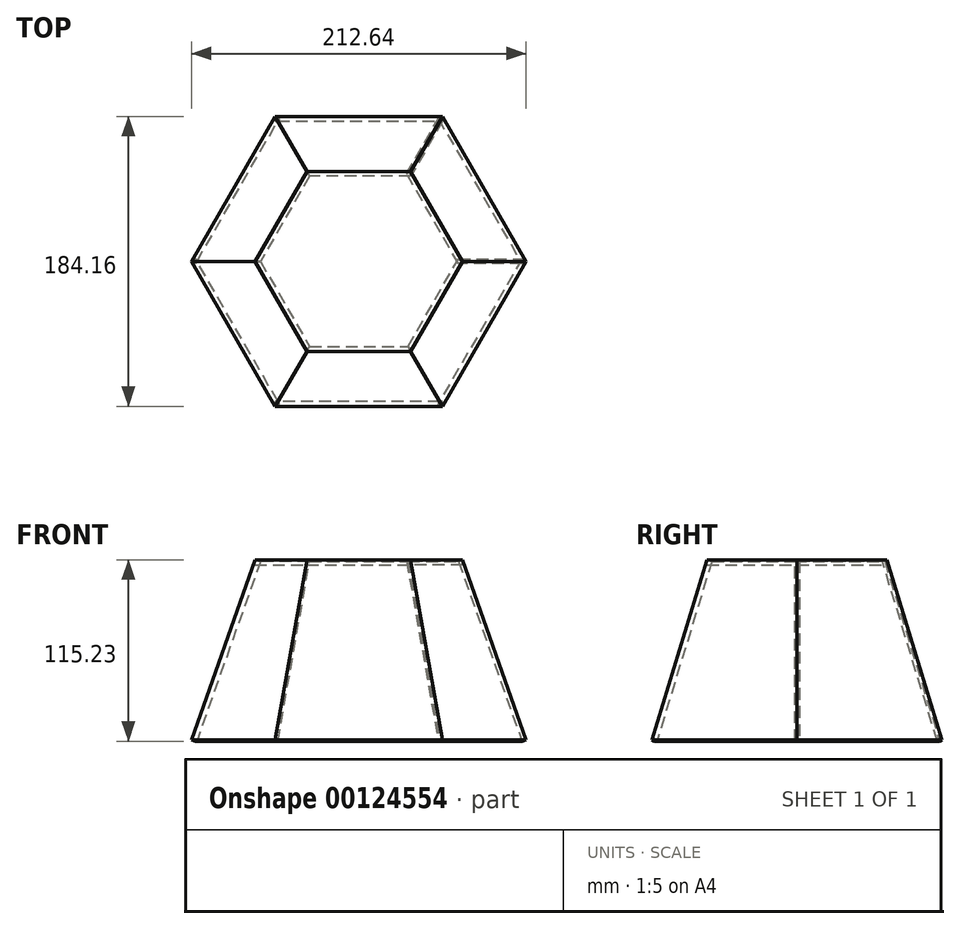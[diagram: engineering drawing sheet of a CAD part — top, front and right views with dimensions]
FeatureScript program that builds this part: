
annotation { "Feature Type Name" : "Feature", "Feature Type Description" : "" }
export const myFeature = defineFeature(function(context is Context, id is Id, definition is map)
    precondition{}
    {
        {
            var Q0;
            Q0=qCreatedBy(makeId("Top.planeOp"),FACE);
            var sketch = newSketch(context, id + "F0", { "sketchPlane" : qUnion([Q0])});
            skCircle(sketch, "E0.cCircle", {"center": v(0, 0) * mm, "radius": 92.08 * mm, "construction": true});
            skLineSegment(sketch, "E0.0", {"start": v(-53.16, 92.08) * mm, "end": v(53.16, 92.08) * mm});
            skLineSegment(sketch, "E0.1", {"start": v(53.16, 92.08) * mm, "end": v(106.32, 0) * mm});
            skLineSegment(sketch, "E0.2", {"start": v(106.32, 0) * mm, "end": v(53.16, -92.07) * mm});
            skLineSegment(sketch, "E0.3", {"start": v(53.16, -92.07) * mm, "end": v(-53.16, -92.08) * mm});
            skLineSegment(sketch, "E0.4", {"start": v(-53.16, -92.08) * mm, "end": v(-106.32, 0) * mm});
            skLineSegment(sketch, "E0.5", {"start": v(-106.32, 0) * mm, "end": v(-53.16, 92.07) * mm});
            skPoint(sketch, "E0.0.midPoint", {"position": v(0, 92.08) * mm});
            skSolve(sketch);
        }
        {
            var Q0;
            Q0=makeQuery(id+"F0.imprint","IMPRINT",FACE,{"disambiguationData":[TD([[makeQuery(id+"F0.imprint","IMPRINT",EDGE,{"derivedFrom":sQuery(id+"F0.wireOp",EDGE,"E0.0")}),-1.0]])]});
            cPlane(context, id + "F1", {"entities" : qUnion([Q0]), "cplaneType" : CPlaneType.OFFSET, "offset" : 114.3 * mm, "width" : 152.4 * mm, "height" : 152.4 * mm});
        }
        {
            var Q0;
            Q0=qCreatedBy(id+"F1.planeOp",FACE);
            var sketch = newSketch(context, id + "F2", { "sketchPlane" : qUnion([Q0])});
            skCircle(sketch, "E1.cCircle", {"center": v(0, 0) * mm, "radius": 57.15 * mm, "construction": true});
            skLineSegment(sketch, "E1.0", {"start": v(-33, 57.15) * mm, "end": v(33, 57.15) * mm});
            skLineSegment(sketch, "E1.1", {"start": v(33, 57.15) * mm, "end": v(66, 0) * mm});
            skLineSegment(sketch, "E1.2", {"start": v(66, 0) * mm, "end": v(33, -57.15) * mm});
            skLineSegment(sketch, "E1.3", {"start": v(33, -57.15) * mm, "end": v(-33, -57.15) * mm});
            skLineSegment(sketch, "E1.4", {"start": v(-33, -57.15) * mm, "end": v(-66, 0) * mm});
            skLineSegment(sketch, "E1.5", {"start": v(-66, 0) * mm, "end": v(-33, 57.15) * mm});
            skPoint(sketch, "E1.0.midPoint", {"position": v(0, 57.15) * mm});
            skSolve(sketch);
        }
        {
            var Q0;
            Q0=sQuery(id+"F0.wireOp",VERTEX,"E0.4.start");
            var Q1;
            Q1=sQuery(id+"F2.wireOp",VERTEX,"E1.4.start");
            var Q2;
            Q2=sQuery(id+"F2.wireOp",VERTEX,"E1.2.end");
            cPlane(context, id + "F3", {"entities" : qUnion([Q0, Q1, Q2]), "cplaneType" : CPlaneType.THREE_POINT, "offset" : 25.4 * mm, "width" : 152.4 * mm, "height" : 152.4 * mm});
        }
        {
            var Q0;
            Q0=qCreatedBy(id+"F3.planeOp",FACE);
            var sketch = newSketch(context, id + "F4", { "sketchPlane" : qUnion([Q0])});
            skLineSegment(sketch, "E2", {"start": v(-53.16, -26.9) * mm, "end": v(-33, 92.61) * mm});
            skLineSegment(sketch, "E3", {"start": v(-33, 92.61) * mm, "end": v(33, 92.61) * mm});
            skLineSegment(sketch, "E4", {"start": v(33, 92.61) * mm, "end": v(53.16, -26.9) * mm});
            skLineSegment(sketch, "E5", {"start": v(53.16, -26.9) * mm, "end": v(-53.16, -26.9) * mm});
            skSolve(sketch);
        }
        {
            var Q0;
            Q0=sQuery(id+"F0.wireOp",VERTEX,"E0.5.start");
            var Q1;
            Q1=sQuery(id+"F4.wireOp",VERTEX,"E2.start");
            var Q2;
            Q2=sQuery(id+"F4.wireOp",VERTEX,"E3.start");
            cPlane(context, id + "F5", {"entities" : qUnion([Q0, Q1, Q2]), "cplaneType" : CPlaneType.THREE_POINT, "offset" : 25.4 * mm, "width" : 152.4 * mm, "height" : 152.4 * mm});
        }
        {
            var Q0;
            Q0=qCreatedBy(id+"F5.planeOp",FACE);
            var sketch = newSketch(context, id + "F6", { "sketchPlane" : qUnion([Q0])});
            skLineSegment(sketch, "E6", {"start": v(47.94, -35.37) * mm, "end": v(47.94, 85.83) * mm});
            skLineSegment(sketch, "E7", {"start": v(47.94, 85.83) * mm, "end": v(-17.13, 96.8) * mm});
            skLineSegment(sketch, "E8", {"start": v(-17.13, 96.8) * mm, "end": v(-56.9, -17.69) * mm});
            skLineSegment(sketch, "E9", {"start": v(-56.9, -17.69) * mm, "end": v(47.94, -35.37) * mm});
            skSolve(sketch);
        }
        {
            var Q0;
            Q0=sQuery(id+"F0.wireOp",VERTEX,"E0.5.end");
            var Q1;
            Q1=sQuery(id+"F6.wireOp",VERTEX,"E9.end");
            var Q2;
            Q2=sQuery(id+"F2.wireOp",VERTEX,"E1.0.start");
            cPlane(context, id + "F7", {"entities" : qUnion([Q0, Q1, Q2]), "cplaneType" : CPlaneType.THREE_POINT, "offset" : 25.4 * mm, "width" : 152.4 * mm, "height" : 152.4 * mm});
        }
        {
            var Q0;
            Q0=qCreatedBy(id+"F7.planeOp",FACE);
            var sketch = newSketch(context, id + "F8", { "sketchPlane" : qUnion([Q0])});
            skLineSegment(sketch, "E10", {"start": v(56.9, -17.69) * mm, "end": v(17.13, 96.8) * mm});
            skLineSegment(sketch, "E11", {"start": v(17.13, 96.8) * mm, "end": v(-47.94, 85.83) * mm});
            skLineSegment(sketch, "E12", {"start": v(-47.94, 85.83) * mm, "end": v(-47.94, -35.37) * mm});
            skLineSegment(sketch, "E13", {"start": v(-47.94, -35.37) * mm, "end": v(56.9, -17.69) * mm});
            skSolve(sketch);
        }
        {
            var Q0;
            Q0=sQuery(id+"F0.wireOp",VERTEX,"E0.5.end");
            var Q1;
            Q1=sQuery(id+"F0.wireOp",VERTEX,"E0.1.start");
            var Q2;
            Q2=sQuery(id+"F2.wireOp",VERTEX,"E1.1.start");
            cPlane(context, id + "F9", {"entities" : qUnion([Q0, Q1, Q2]), "cplaneType" : CPlaneType.THREE_POINT, "offset" : 25.4 * mm, "width" : 152.4 * mm, "height" : 152.4 * mm});
        }
        {
            var Q0;
            Q0=qCreatedBy(id+"F9.planeOp",FACE);
            var sketch = newSketch(context, id + "F10", { "sketchPlane" : qUnion([Q0])});
            skLineSegment(sketch, "E14", {"start": v(53.16, -26.9) * mm, "end": v(-53.16, -26.9) * mm});
            skLineSegment(sketch, "E15", {"start": v(-53.16, -26.9) * mm, "end": v(-33, 92.61) * mm});
            skLineSegment(sketch, "E16", {"start": v(-33, 92.61) * mm, "end": v(33, 92.61) * mm});
            skLineSegment(sketch, "E17", {"start": v(33, 92.61) * mm, "end": v(53.16, -26.9) * mm});
            skSolve(sketch);
        }
        {
            var Q0;
            Q0=sQuery(id+"F10.wireOp",VERTEX,"E15.start");
            var Q1;
            Q1=sQuery(id+"F0.wireOp",VERTEX,"E0.2.start");
            var Q2;
            Q2=sQuery(id+"F2.wireOp",VERTEX,"E1.2.start");
            cPlane(context, id + "F11", {"entities" : qUnion([Q0, Q1, Q2]), "cplaneType" : CPlaneType.THREE_POINT, "offset" : 25.4 * mm, "width" : 152.4 * mm, "height" : 152.4 * mm});
        }
        {
            var Q0;
            Q0=qCreatedBy(id+"F11.planeOp",FACE);
            var sketch = newSketch(context, id + "F12", { "sketchPlane" : qUnion([Q0])});
            skLineSegment(sketch, "E18", {"start": v(-47.94, -35.37) * mm, "end": v(-47.94, 85.83) * mm});
            skLineSegment(sketch, "E19", {"start": v(-47.94, 85.83) * mm, "end": v(17.13, 96.8) * mm});
            skLineSegment(sketch, "E20", {"start": v(17.13, 96.8) * mm, "end": v(56.9, -17.69) * mm});
            skLineSegment(sketch, "E21", {"start": v(56.9, -17.69) * mm, "end": v(-47.94, -35.37) * mm});
            skSolve(sketch);
        }
        {
            var Q0;
            Q0=sQuery(id+"F12.wireOp",VERTEX,"E18.start");
            var Q1;
            Q1=sQuery(id+"F4.wireOp",VERTEX,"E5.start");
            var Q2;
            Q2=sQuery(id+"F4.wireOp",VERTEX,"E4.start");
            cPlane(context, id + "F13", {"entities" : qUnion([Q0, Q1, Q2]), "cplaneType" : CPlaneType.THREE_POINT, "offset" : 25.4 * mm, "width" : 152.4 * mm, "height" : 152.4 * mm});
        }
        {
            var Q0;
            Q0=qCreatedBy(id+"F13.planeOp",FACE);
            var sketch = newSketch(context, id + "F14", { "sketchPlane" : qUnion([Q0])});
            skLineSegment(sketch, "E22", {"start": v(-56.9, -17.69) * mm, "end": v(-17.13, 96.8) * mm});
            skLineSegment(sketch, "E23", {"start": v(-17.13, 96.8) * mm, "end": v(47.94, 85.83) * mm});
            skLineSegment(sketch, "E24", {"start": v(47.94, 85.83) * mm, "end": v(47.94, -35.37) * mm});
            skLineSegment(sketch, "E25", {"start": v(47.94, -35.37) * mm, "end": v(-56.9, -17.69) * mm});
            skSolve(sketch);
        }
        {
            var Q0;
            Q0=makeQuery(id+"F14.imprint","IMPRINT",FACE,{"disambiguationData":[TD([[makeQuery(id+"F14.imprint","IMPRINT",EDGE,{"derivedFrom":sQuery(id+"F14.wireOp",EDGE,"E22")}),-1.0]])]});
            extrude(context, id + "F15", {"entities" : qUnion([Q0]), "oppositeDirection" : true, "depth" : 3.17 * mm});
        }
        {
            var Q0;
            Q0=makeQuery(id+"F4.imprint","IMPRINT",FACE,{"disambiguationData":[TD([[makeQuery(id+"F4.imprint","IMPRINT",EDGE,{"derivedFrom":sQuery(id+"F4.wireOp",EDGE,"E2")}),-1.0]])]});
            extrude(context, id + "F16", {"entities" : qUnion([Q0]), "operationType" : NewBodyOperationType.ADD, "oppositeDirection" : true, "depth" : 3.17 * mm});
        }
        {
            var Q0;
            Q0=makeQuery(id+"F6.imprint","IMPRINT",FACE,{"disambiguationData":[TD([[makeQuery(id+"F6.imprint","IMPRINT",EDGE,{"derivedFrom":sQuery(id+"F6.wireOp",EDGE,"E6")}),1.0]])]});
            extrude(context, id + "F17", {"entities" : qUnion([Q0]), "operationType" : NewBodyOperationType.ADD, "depth" : 3.17 * mm});
        }
        {
            var Q0;
            Q0=makeQuery(id+"F8.imprint","IMPRINT",FACE,{"disambiguationData":[TD([[makeQuery(id+"F8.imprint","IMPRINT",EDGE,{"derivedFrom":sQuery(id+"F8.wireOp",EDGE,"E10")}),1.0]])]});
            extrude(context, id + "F18", {"entities" : qUnion([Q0]), "operationType" : NewBodyOperationType.ADD, "depth" : 3.17 * mm});
        }
        {
            var Q0;
            Q0=makeQuery(id+"F10.imprint","IMPRINT",FACE,{"disambiguationData":[TD([[makeQuery(id+"F10.imprint","IMPRINT",EDGE,{"derivedFrom":sQuery(id+"F10.wireOp",EDGE,"E14")}),-1.0]])]});
            extrude(context, id + "F19", {"entities" : qUnion([Q0]), "operationType" : NewBodyOperationType.ADD, "oppositeDirection" : true, "depth" : 3.17 * mm});
        }
        {
            var Q0;
            Q0=makeQuery(id+"F12.imprint","IMPRINT",FACE,{"disambiguationData":[TD([[makeQuery(id+"F12.imprint","IMPRINT",EDGE,{"derivedFrom":sQuery(id+"F12.wireOp",EDGE,"E18")}),-1.0]])]});
            extrude(context, id + "F20", {"entities" : qUnion([Q0]), "oppositeDirection" : true, "depth" : 3.17 * mm});
        }
        {
            var Q0;
            Q0=makeQuery(id+"F2.imprint","IMPRINT",FACE,{"disambiguationData":[TD([[makeQuery(id+"F2.imprint","IMPRINT",EDGE,{"derivedFrom":sQuery(id+"F2.wireOp",EDGE,"E1.0")}),-1.0]])]});
            extrude(context, id + "F21", {"entities" : qUnion([Q0]), "oppositeDirection" : true, "depth" : 3.17 * mm});
        }
        {
            var Q0;
            Q0=makeQuery(id+"F19.opExtrude","CAP_FACE",FACE,{"disambiguationData":[OSD([sQuery(id+"F10.wireOp",EDGE,"E14"),sQuery(id+"F10.wireOp",EDGE,"E15"),sQuery(id+"F10.wireOp",EDGE,"E16"),sQuery(id+"F10.wireOp",EDGE,"E17")])],"isStart":true});
            var sketch = newSketch(context, id + "F22", { "sketchPlane" : qUnion([Q0])});
            skLineSegment(sketch, "E26.bottom", {"start": v(25.5, 62.72) * mm, "end": v(-25.5, 62.72) * mm});
            skLineSegment(sketch, "E26.top", {"start": v(25.5, 11.72) * mm, "end": v(-25.5, 11.72) * mm});
            skLineSegment(sketch, "E26.left", {"start": v(25.5, 62.72) * mm, "end": v(25.5, 11.72) * mm});
            skLineSegment(sketch, "E26.right", {"start": v(-25.5, 62.72) * mm, "end": v(-25.5, 11.72) * mm});
            skPoint(sketch, "E26.middle", {"position": v(0, 37.22) * mm});
            skSolve(sketch);
        }
        {
            var Q0;
            Q0 = qSketchRegion(id + "F22", true);
            extrude(context, id + "F23", {"entities" : qUnion([Q0]), "operationType" : NewBodyOperationType.ADD, "oppositeDirection" : true, "depth" : 3 * mm});
        }
    });
